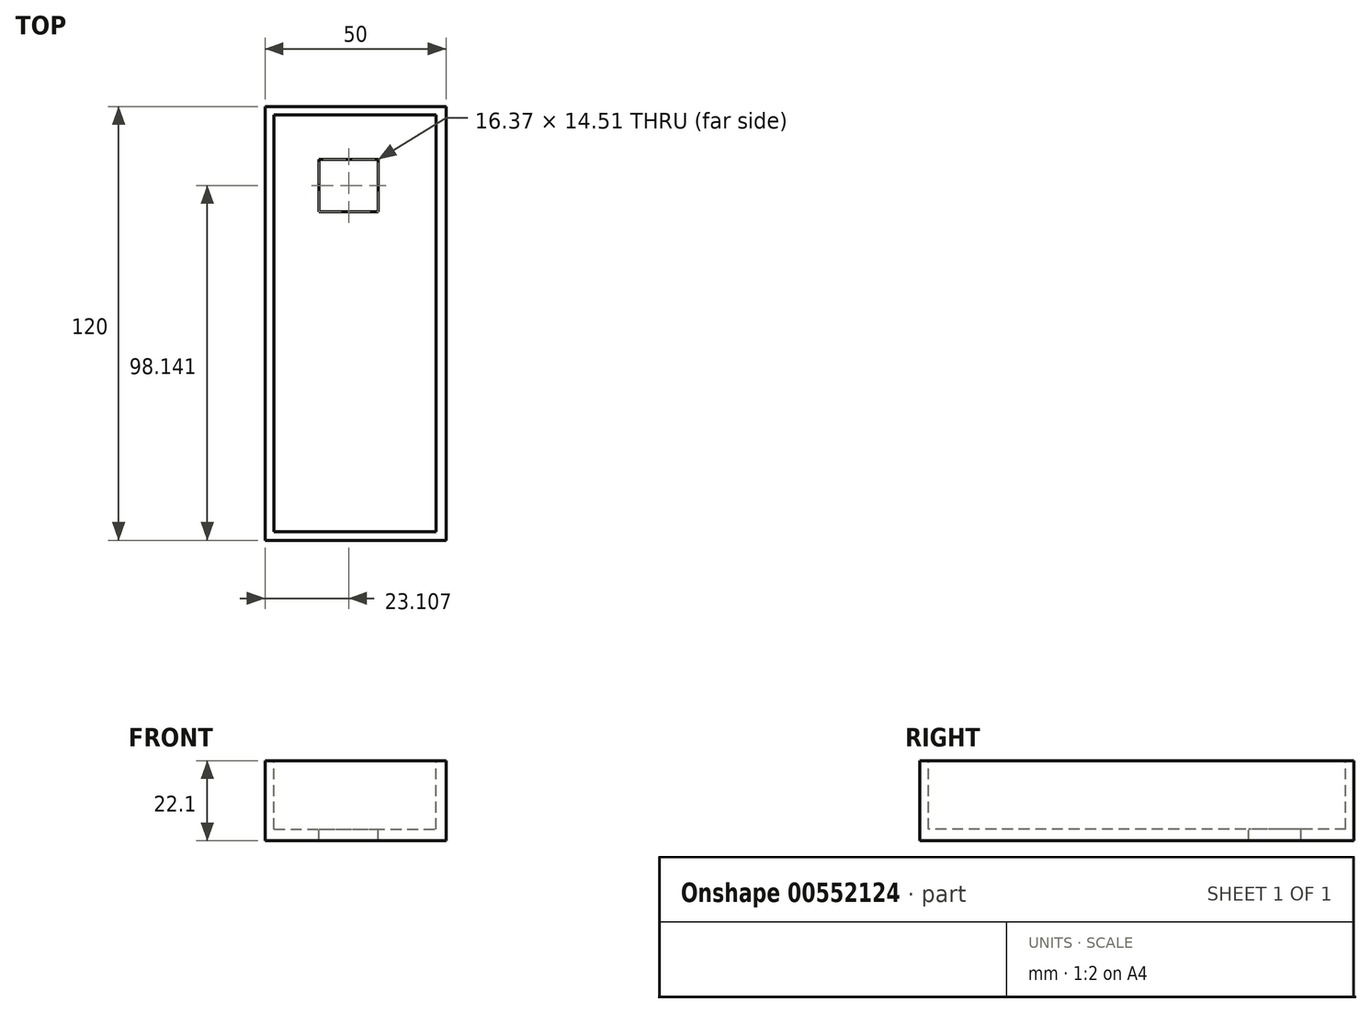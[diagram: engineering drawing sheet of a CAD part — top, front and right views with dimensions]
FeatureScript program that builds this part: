
annotation { "Feature Type Name" : "Feature", "Feature Type Description" : "" }
export const myFeature = defineFeature(function(context is Context, id is Id, definition is map)
    precondition{}
    {
        {
            var Q0;
            Q0=qCreatedBy(makeId("Top.planeOp"),FACE);
            var sketch = newSketch(context, id + "F0", { "sketchPlane" : qUnion([Q0])});
            skLineSegment(sketch, "E0.bottom", {"start": v(0, 0) * mm, "end": v(50, 0) * mm});
            skLineSegment(sketch, "E0.top", {"start": v(0, 120) * mm, "end": v(50, 120) * mm});
            skLineSegment(sketch, "E0.left", {"start": v(0, 0) * mm, "end": v(0, 120) * mm});
            skLineSegment(sketch, "E0.right", {"start": v(50, 0) * mm, "end": v(50, 120) * mm});
            skSolve(sketch);
        }
        {
            var Q0;
            Q0 = qSketchRegion(id + "F0", true);
            extrude(context, id + "F1", {"entities" : qUnion([Q0]), "depth" : 22.1 * mm, "offsetDistance" : 25 * mm});
        }
        {
            var Q0;
            Q0=makeQuery(id+"F1.opExtrude","CAP_FACE",FACE,{"disambiguationData":[OSD([sQuery(id+"F0.wireOp",EDGE,"E0.bottom"),sQuery(id+"F0.wireOp",EDGE,"E0.top"),sQuery(id+"F0.wireOp",EDGE,"E0.left"),sQuery(id+"F0.wireOp",EDGE,"E0.right")])],"isStart":false});
            var sketch = newSketch(context, id + "F2", { "sketchPlane" : qUnion([Q0])});
            skLineSegment(sketch, "E1.bottom", {"start": v(2.48, 117.77) * mm, "end": v(47.27, 117.77) * mm});
            skLineSegment(sketch, "E1.top", {"start": v(2.48, 2.4) * mm, "end": v(47.27, 2.4) * mm});
            skLineSegment(sketch, "E1.left", {"start": v(2.48, 117.77) * mm, "end": v(2.48, 2.4) * mm});
            skLineSegment(sketch, "E1.right", {"start": v(47.27, 117.77) * mm, "end": v(47.27, 2.4) * mm});
            skSolve(sketch);
        }
        {
            var Q0;
            Q0 = qSketchRegion(id + "F2", true);
            extrude(context, id + "F3", {"entities" : qUnion([Q0]), "operationType" : NewBodyOperationType.REMOVE, "oppositeDirection" : true, "depth" : 18.9 * mm, "offsetDistance" : 25 * mm});
        }
        {
            var Q0;
            Q0=makeQuery(id+"F3.boolean.opBoolean","COPY",FACE,{"derivedFrom":makeQuery(id+"F3.opExtrude","CAP_FACE",FACE,{"disambiguationData":[OSD([sQuery(id+"F2.wireOp",EDGE,"E1.bottom"),sQuery(id+"F2.wireOp",EDGE,"E1.top"),sQuery(id+"F2.wireOp",EDGE,"E1.left"),sQuery(id+"F2.wireOp",EDGE,"E1.right")])],"isStart":false})});
            var sketch = newSketch(context, id + "F4", { "sketchPlane" : qUnion([Q0])});
            skLineSegment(sketch, "E2.bottom", {"start": v(14.92, 105.4) * mm, "end": v(31.3, 105.4) * mm});
            skLineSegment(sketch, "E2.top", {"start": v(14.92, 90.89) * mm, "end": v(31.3, 90.89) * mm});
            skLineSegment(sketch, "E2.left", {"start": v(14.92, 105.4) * mm, "end": v(14.92, 90.89) * mm});
            skLineSegment(sketch, "E2.right", {"start": v(31.3, 105.4) * mm, "end": v(31.3, 90.89) * mm});
            skSolve(sketch);
        }
        {
            var Q0;
            Q0 = qSketchRegion(id + "F4", true);
            extrude(context, id + "F5", {"entities" : qUnion([Q0]), "operationType" : NewBodyOperationType.REMOVE, "endBound" : BoundingType.UP_TO_NEXT, "oppositeDirection" : true, "depth" : 25 * mm, "offsetDistance" : 25 * mm});
        }
    });
